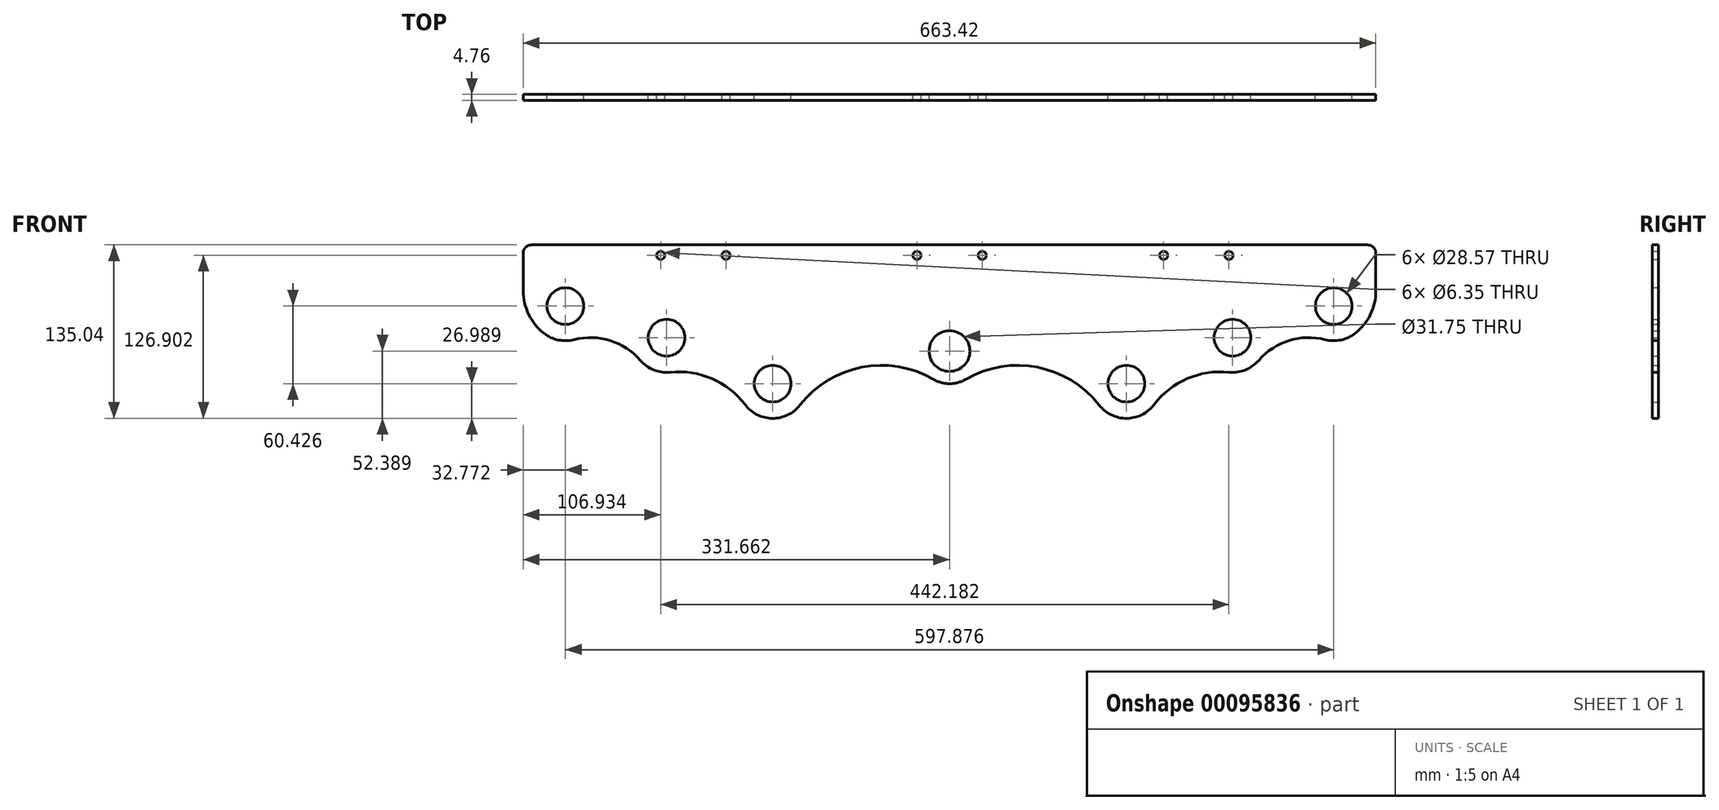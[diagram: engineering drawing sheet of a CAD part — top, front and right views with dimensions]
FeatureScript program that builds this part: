
annotation { "Feature Type Name" : "Feature", "Feature Type Description" : "" }
export const myFeature = defineFeature(function(context is Context, id is Id, definition is map)
    precondition{}
    {
        {
            var Q0;
            Q0=qCreatedBy(makeId("Front.planeOp"),FACE);
            var sketch = newSketch(context, id + "F0", { "sketchPlane" : qUnion([Q0])});
            skLineSegment(sketch, "E0", {"start": v(678.42, -37.96) * mm, "end": v(-454, -37.96) * mm, "construction": true});
            skCircle(sketch, "E1", {"center": v(298.94, 73.27) * mm, "radius": 41.28 * mm, "construction": true});
            skLineSegment(sketch, "E2", {"start": v(0, -37.96) * mm, "end": v(0, 332.54) * mm, "construction": true});
            skCircle(sketch, "E3", {"center": v(298.94, 73.27) * mm, "radius": 14.29 * mm});
            skCircle(sketch, "E4", {"center": v(217.4, 112.75) * mm, "radius": 3.18 * mm});
            skCircle(sketch, "E5", {"center": v(166.6, 112.75) * mm, "radius": 3.18 * mm});
            skCircle(sketch, "E6", {"center": v(25.4, 112.75) * mm, "radius": 3.18 * mm});
            skLineSegment(sketch, "E7", {"start": v(331.7, 85.13) * mm, "end": v(331.7, 114.54) * mm});
            skPoint(sketch, "E8.visualSharp", {"position": v(331.7, 119.1) * mm});
            skArc(sketch, "E8.filletArc", {"start": v(331.7, 114.54) * mm, "mid": v(329.85, 119.03) * mm, "end": v(325.36, 120.9) * mm});
            skPoint(sketch, "E9.third.point", {"position": v(216.25, -1.48) * mm});
            skPoint(sketch, "E10.orphan", {"position": v(0, -22.86) * mm});
            skCircle(sketch, "E11", {"center": v(298.94, 73.27) * mm, "radius": 21 * mm, "construction": true});
            skCircle(sketch, "E12", {"center": v(-0.05, 38.24) * mm, "radius": 41.28 * mm, "construction": true});
            skCircle(sketch, "E13.MirrorC", {"center": v(-0.05, 38.24) * mm, "radius": 15.88 * mm});
            skLineSegment(sketch, "E14", {"start": v(325.36, 120.9) * mm, "end": v(0, 120.9) * mm});
            skLineSegment(sketch, "E15.MirrorCS", {"start": v(-325.36, 120.9) * mm, "end": v(0, 120.9) * mm});
            skArc(sketch, "E16.MirrorCS", {"start": v(-331.7, 114.54) * mm, "mid": v(-329.85, 119.03) * mm, "end": v(-325.36, 120.9) * mm});
            skLineSegment(sketch, "E17.MirrorCS", {"start": v(-331.7, 85.13) * mm, "end": v(-331.7, 114.54) * mm});
            skCircle(sketch, "E18.MirrorC", {"center": v(-25.4, 112.75) * mm, "radius": 3.18 * mm});
            skCircle(sketch, "E19.MirrorC", {"center": v(-173.98, 112.75) * mm, "radius": 3.18 * mm});
            skCircle(sketch, "E20.MirrorC", {"center": v(-224.78, 112.75) * mm, "radius": 3.18 * mm});
            skCircle(sketch, "E21", {"center": v(220.2, 48.65) * mm, "radius": 50.8 * mm, "construction": true});
            skCircle(sketch, "E22", {"center": v(137.63, 12.84) * mm, "radius": 50.8 * mm, "construction": true});
            skLineSegment(sketch, "E23", {"start": v(338.06, -37.96) * mm, "end": v(720.92, -140.55) * mm, "construction": true});
            skLineSegment(sketch, "E24", {"start": v(338.06, -37.96) * mm, "end": v(354.5, 23.38) * mm, "construction": true});
            skLineSegment(sketch, "E25", {"start": v(354.5, 23.38) * mm, "end": v(391.3, 13.51) * mm, "construction": true});
            skLineSegment(sketch, "E26", {"start": v(391.3, 13.51) * mm, "end": v(374.86, -47.82) * mm, "construction": true});
            skLineSegment(sketch, "E27", {"start": v(338.06, -37.96) * mm, "end": v(368.5, 75.63) * mm, "construction": true});
            skLineSegment(sketch, "E28", {"start": v(368.5, 75.63) * mm, "end": v(497.3, 41.12) * mm, "construction": true});
            skLineSegment(sketch, "E29", {"start": v(497.3, 41.12) * mm, "end": v(466.86, -72.47) * mm, "construction": true});
            skLineSegment(sketch, "E30", {"start": v(338.06, -37.96) * mm, "end": v(1103.17, -37.96) * mm});
            skCircle(sketch, "E31", {"center": v(220.2, 48.65) * mm, "radius": 14.29 * mm});
            skCircle(sketch, "E32", {"center": v(220.2, 48.65) * mm, "radius": 21 * mm, "construction": true});
            skCircle(sketch, "E33", {"center": v(137.63, 12.84) * mm, "radius": 14.29 * mm});
            skCircle(sketch, "E34", {"center": v(137.63, 12.84) * mm, "radius": 21 * mm, "construction": true});
            skCircle(sketch, "E35", {"center": v(-0.05, 38.24) * mm, "radius": 140 * mm, "construction": true});
            skCircle(sketch, "E36", {"center": v(137.63, 12.84) * mm, "radius": 90 * mm, "construction": true});
            skCircle(sketch, "E37", {"center": v(220.2, 48.65) * mm, "radius": 82.5 * mm, "construction": true});
            skLineSegment(sketch, "E38", {"start": v(220.2, 48.65) * mm, "end": v(298.94, 73.27) * mm, "construction": true});
            skLineSegment(sketch, "E39", {"start": v(259.57, 60.96) * mm, "end": v(264.11, 46.41) * mm, "construction": true});
            skArc(sketch, "E40.0", {"start": v(292.21, 47.13) * mm, "mid": v(304.46, 46.85) * mm, "end": v(315.57, 52.01) * mm});
            skArc(sketch, "E41.0", {"start": v(217.46, 21.8) * mm, "mid": v(230.16, 23.57) * mm, "end": v(240.61, 31) * mm});
            skArc(sketch, "E42.0", {"start": v(116.37, -3.78) * mm, "mid": v(137.8, -14.15) * mm, "end": v(159.1, -3.51) * mm});
            skCircle(sketch, "E43", {"center": v(-0.05, 38.24) * mm, "radius": 21 * mm, "construction": true});
            skArc(sketch, "E44.0", {"start": v(12.69, 16.26) * mm, "mid": v(6.57, 13.72) * mm, "end": v(0, 12.84) * mm});
            skArc(sketch, "E45", {"start": v(292.21, 47.13) * mm, "mid": v(264.11, 46.41) * mm, "end": v(240.61, 31) * mm});
            skLineSegment(sketch, "E46", {"start": v(137.63, 12.84) * mm, "end": v(220.2, 48.65) * mm, "construction": true});
            skLineSegment(sketch, "E47", {"start": v(178.91, 30.75) * mm, "end": v(184.98, 16.76) * mm});
            skArc(sketch, "E48", {"start": v(217.46, 21.8) * mm, "mid": v(184.98, 16.76) * mm, "end": v(159.1, -3.51) * mm});
            skLineSegment(sketch, "E49", {"start": v(-0.05, 38.24) * mm, "end": v(137.63, 12.84) * mm, "construction": true});
            skLineSegment(sketch, "E50", {"start": v(68.8, 25.54) * mm, "end": v(68.8, 25.54) * mm});
            skArc(sketch, "E51", {"start": v(116.37, -3.78) * mm, "mid": v(68.28, 25.64) * mm, "end": v(12.69, 16.26) * mm});
            skArc(sketch, "E52", {"start": v(315.57, 52.01) * mm, "mid": v(327.46, 66.7) * mm, "end": v(331.7, 85.13) * mm});
            skCircle(sketch, "E53.MirrorC", {"center": v(-137.63, 12.84) * mm, "radius": 14.29 * mm});
            skCircle(sketch, "E54.MirrorC", {"center": v(-220.2, 48.65) * mm, "radius": 14.29 * mm});
            skCircle(sketch, "E55.MirrorC", {"center": v(-298.94, 73.27) * mm, "radius": 14.29 * mm});
            skArc(sketch, "E56.MirrorCS", {"start": v(-315.57, 52.01) * mm, "mid": v(-327.46, 66.7) * mm, "end": v(-331.7, 85.13) * mm});
            skArc(sketch, "E57.MirrorCS", {"start": v(-292.21, 47.13) * mm, "mid": v(-304.46, 46.85) * mm, "end": v(-315.57, 52.01) * mm});
            skArc(sketch, "E58.MirrorCS", {"start": v(-292.21, 47.13) * mm, "mid": v(-264.11, 46.41) * mm, "end": v(-240.61, 31) * mm});
            skArc(sketch, "E59.MirrorCS", {"start": v(-217.46, 21.8) * mm, "mid": v(-230.16, 23.57) * mm, "end": v(-240.61, 31) * mm});
            skArc(sketch, "E60.MirrorCS", {"start": v(-217.46, 21.8) * mm, "mid": v(-184.98, 16.76) * mm, "end": v(-159.1, -3.51) * mm});
            skArc(sketch, "E61.MirrorCS", {"start": v(-116.37, -3.78) * mm, "mid": v(-137.8, -14.15) * mm, "end": v(-159.1, -3.51) * mm});
            skArc(sketch, "E62.MirrorCS", {"start": v(-116.37, -3.78) * mm, "mid": v(-68.28, 25.64) * mm, "end": v(-12.69, 16.26) * mm});
            skCircle(sketch, "E63.MirrorC", {"center": v(-137.63, 12.84) * mm, "radius": 50.8 * mm, "construction": true});
            skCircle(sketch, "E64.MirrorC", {"center": v(-220.2, 48.65) * mm, "radius": 50.8 * mm, "construction": true});
            skCircle(sketch, "E65.MirrorC", {"center": v(-298.94, 73.27) * mm, "radius": 41.28 * mm, "construction": true});
            skArc(sketch, "E66.MirrorCS", {"start": v(-12.69, 16.26) * mm, "mid": v(-6.57, 13.72) * mm, "end": v(0, 12.84) * mm});
            skLineSegment(sketch, "E67", {"start": v(158.05, -33.67) * mm, "end": v(315.53, 35.47) * mm, "construction": true});
            skSolve(sketch);
        }
        {
            var Q0;
            Q0=makeQuery(id+"F0.imprint","IMPRINT",FACE,{"disambiguationData":[TD([[makeQuery(id+"F0.imprint","IMPRINT",EDGE,{"derivedFrom":sQuery(id+"F0.wireOp",EDGE,"E3")}),-1.0]])]});
            extrude(context, id + "F1", {"entities" : qUnion([Q0]), "depth" : 4.76 * mm});
        }
    });
